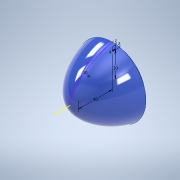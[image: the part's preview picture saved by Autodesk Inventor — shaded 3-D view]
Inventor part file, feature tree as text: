
AUTODESK INVENTOR PART (.ipt)
format: ipt  version: 2020 (Build 240168000, 168)  size: 275,968 bytes
history: native  units: mm
features: sketch x1, revolve x1
ambient origin geometry x8: Origin, YZ Plane, XZ Plane, XY Plane, X Axis, Y Axis, Z Axis, Center Point
bodies: Body1 (feature_tree)
feature tree (2):
  sketch  "Sketch1"  dims[d44=10.0mm d45=5.0mm d46=4.0mm d47=5.0mm d48=90.0deg d49=30.0mm d50=40.0mm d51=10.0mm d11=0.872665mm d12=0.872665mm]
  revolve  "Revolution3"  [1 undecoded]
note: 1 required parameter value undecoded (feature->parameter linkage not recoverable at this tier; creation-order binding heuristic only, values carry confidence <= 0.55)
